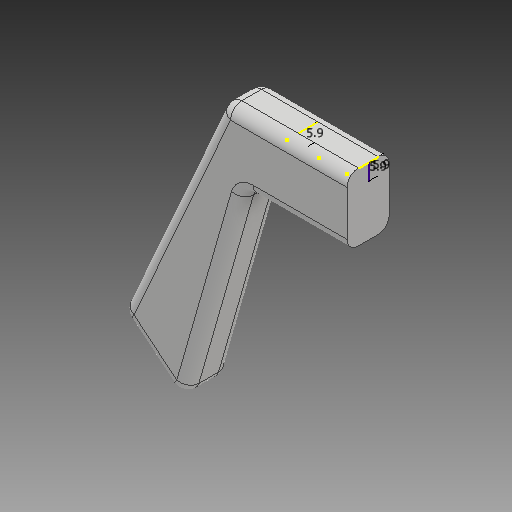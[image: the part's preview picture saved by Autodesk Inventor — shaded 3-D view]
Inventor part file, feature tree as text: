
AUTODESK INVENTOR PART (.ipt)
format: ipt  version: 2018 (Build 220112000, 112)  size: 185,344 bytes
history: native  units: mm
features: sketch x7, extrude x3, fillet x1
ambient origin geometry x8: Origin, YZ Plane, XZ Plane, XY Plane, X Axis, Y Axis, Z Axis, Center Point
bodies: Body1 (feature_tree), Body2 (feature_tree), Body3 (feature_tree)
feature tree (11):
  extrude  "Extrusion3"  Depth=24.0mm
  fillet  "Fillet3"  Radius=24.0mm
  sketch  "Sketch5"  dims[d44=28.8mm d45=4.0mm]
  extrude  "Extrusion4"  Depth=4.0mm
  sketch  "Sketch7"  dims[d49=5.9mm]
  extrude  "Extrusion5"  Depth=4.0mm
  sketch  "Sketch9"  dims[d54=10.0mm d55=0.0mm]
  sketch  "Sketch10"  dims[d56=5.9mm d57=5.9mm]
  sketch  "Sketch4"  dims[d40=22.5mm d41=90.0mm d43=24.0mm]
  sketch  "Sketch6"  dims[d46=15.0mm d47=0.0mm d48=4.0mm]
  sketch  "Sketch8"  dims[d50=11.5mm d51=0.0mm]
